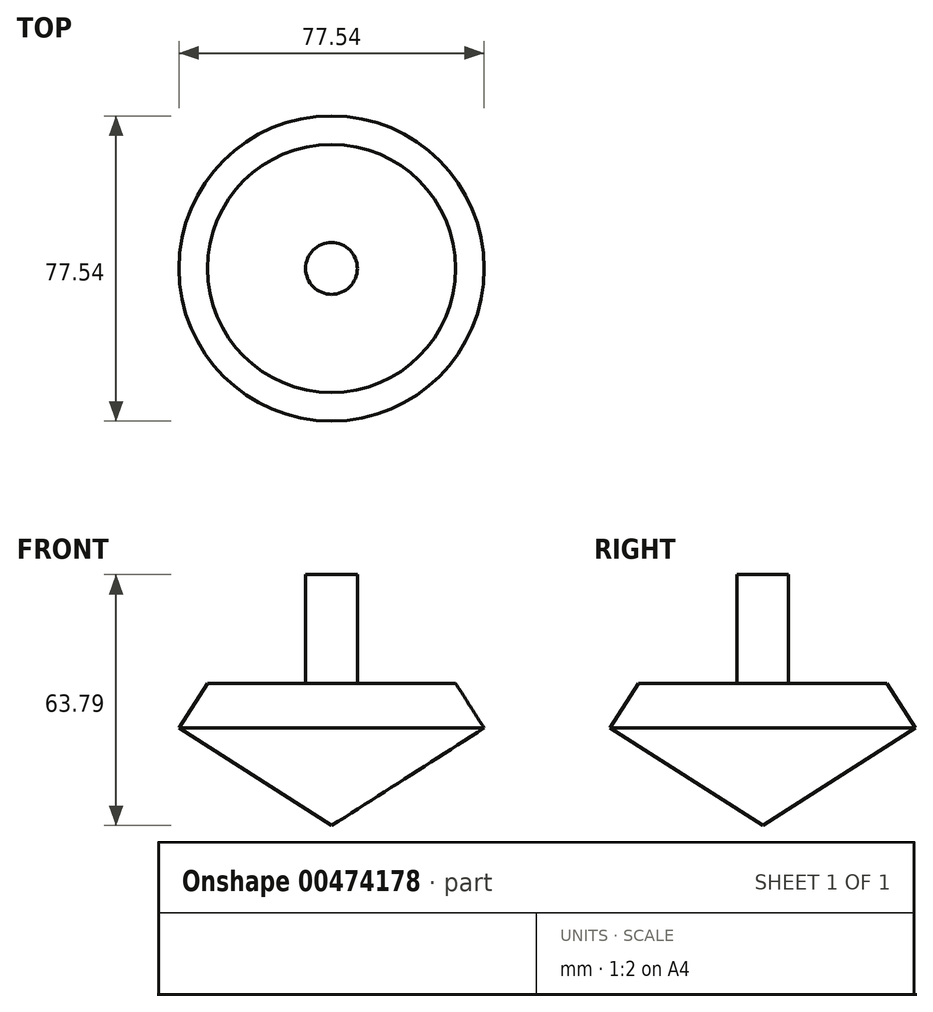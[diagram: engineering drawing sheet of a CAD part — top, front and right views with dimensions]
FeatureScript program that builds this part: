
annotation { "Feature Type Name" : "Feature", "Feature Type Description" : "" }
export const myFeature = defineFeature(function(context is Context, id is Id, definition is map)
    precondition{}
    {
        {
            var Q0;
            Q0=qCreatedBy(makeId("Front.planeOp"),FACE);
            var sketch = newSketch(context, id + "F0", { "sketchPlane" : qUnion([Q0])});
            skLineSegment(sketch, "E0", {"start": v(0, 0) * mm, "end": v(38.77, 24.8) * mm});
            skLineSegment(sketch, "E1", {"start": v(38.77, 24.8) * mm, "end": v(31.52, 36.15) * mm});
            skLineSegment(sketch, "E2", {"start": v(31.52, 36.15) * mm, "end": v(6.57, 36.15) * mm});
            skLineSegment(sketch, "E3", {"start": v(6.57, 36.15) * mm, "end": v(6.57, 51.1) * mm});
            skLineSegment(sketch, "E4", {"start": v(6.57, 51.1) * mm, "end": v(0, 51.1) * mm});
            skLineSegment(sketch, "E5", {"start": v(0, 51.1) * mm, "end": v(0, 0) * mm});
            skSolve(sketch);
        }
        {
            var Q0;
            Q0 = qSketchRegion(id + "F0", true);
            var Q1;
            Q1=sQuery(id+"F0.wireOp",EDGE,"E5");
            revolve(context, id + "F1", {"entities" : qUnion([Q0]), "axis" : qUnion([Q1]), "revolveType" : RevolveType.FULL});
        }
        {
            var Q0;
            Q0=makeQuery(id+"F1.opRevolve","SWEPT_FACE",FACE,{"disambiguationData":[OSD([sQuery(id+"F0.wireOp",EDGE,"E4")])]});
            extrude(context, id + "F2", {"entities" : qUnion([Q0]), "operationType" : NewBodyOperationType.ADD, "depth" : 12.7 * mm});
        }
    });
